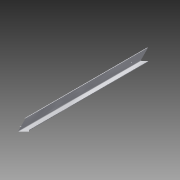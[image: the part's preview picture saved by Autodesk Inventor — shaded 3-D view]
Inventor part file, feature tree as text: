
AUTODESK INVENTOR PART (.ipt)
format: ipt  version: 2015 SP1 (Build 190203100, 203)  size: 150,528 bytes
history: native  units: in
note: dims shown in document units (in); Inventor stores cm internally (conversion verified against a paired STEP export)
features: sketch x6, hole x4, extrude x2, fillet x1, projected_geometry x1
ambient origin geometry x8: Origin, YZ Plane, XZ Plane, XY Plane, X Axis, Y Axis, Z Axis, Center Point
bodies: Solid1 (feature_tree)
feature tree (14):
  extrude  "Extrusion1"  Depth=2.0in
  hole  "Hole1"  [1 undecoded]
  hole  "Hole2"  [1 undecoded]
  hole  "Hole3"  [1 undecoded]
  fillet  "Fillet1"  Radius=8.0in
  hole  "Hole5"  [1 undecoded]
  extrude  "Extrusion2"  Depth=1.0in
  sketch  "Sketch1"  dims[d0=0.125in d1=2.0in]
  sketch  "Sketch2"  dims[d2=2.0in d3=0.125in]
  sketch  "Sketch3"  dims[d4=38.0in d5=0.0in d6=0.9375in]
  sketch  "Sketch4"  dims[d7=0.9375in d8=0.5in d9=8.0in]
  sketch  "Sketch6"  dims[d10=0.25in d11=0.75in d12=0.375in d13=0.25in d14=0.5635in d15=1.0in d16=0.8108in d17=0.9375in]
  sketch  "Sketch8"  dims[d19=0.375in d20=0.75in d21=0.375in d22=0.25in d23=0.5635in d24=1.0in d25=0.8108in d26=35.0in d27=0.6875in d28=2.0in d29=0.25in d30=0.75in d31=0.375in d32=0.25in d33=0.5635in d34=1.0in d35=0.8108in d36=0.125in d49=1.5in d50=0.5in d51=1.25in d52=0.5in d53=0.1875in d54=0.75in d55=0.375in d56=0.25in d57=0.5635in d58=1.0in d59=0.8108in d60=0.875in d61=4.0in d62=4.0in d63=45.0deg d64=45.0deg d65=1.0in d66=0.0in]
  projected_geometry  "Projected Loop1"
note: 4 required parameter values undecoded (feature->parameter linkage not recoverable at this tier; creation-order binding heuristic only, values carry confidence <= 0.55)
